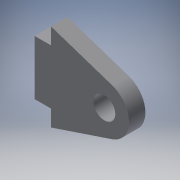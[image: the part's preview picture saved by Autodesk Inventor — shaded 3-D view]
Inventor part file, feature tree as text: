
AUTODESK INVENTOR PART (.ipt)
format: ipt  version: 2018 (Build 220112000, 112)  size: 108,032 bytes
history: native  units: in
note: dims shown in document units (in); Inventor stores cm internally (conversion verified against a paired STEP export)
features: other x3, reference x2, extrude x1, sketch x1
ambient origin geometry x8: Origin, YZ Plane, XZ Plane, XY Plane, X Axis, Y Axis, Z Axis, Center Point
bodies: Body1 (feature_tree)
feature tree (7):
  extrude  "Extrusion2"  Depth=0.1181in
  sketch  "Sketch1"  dims[d0=0.3543in d1=0.3839in d2=0.315in d3=0.1969in d4=0.1969in d5=0.1181in d12=0.1181in d13=0.0in]
  reference  "Reference1"
  reference  "Reference2"
  other  "Bearing Support.iam"
  other  "Bearing:1"
  other  "Washers 4mm:1"
